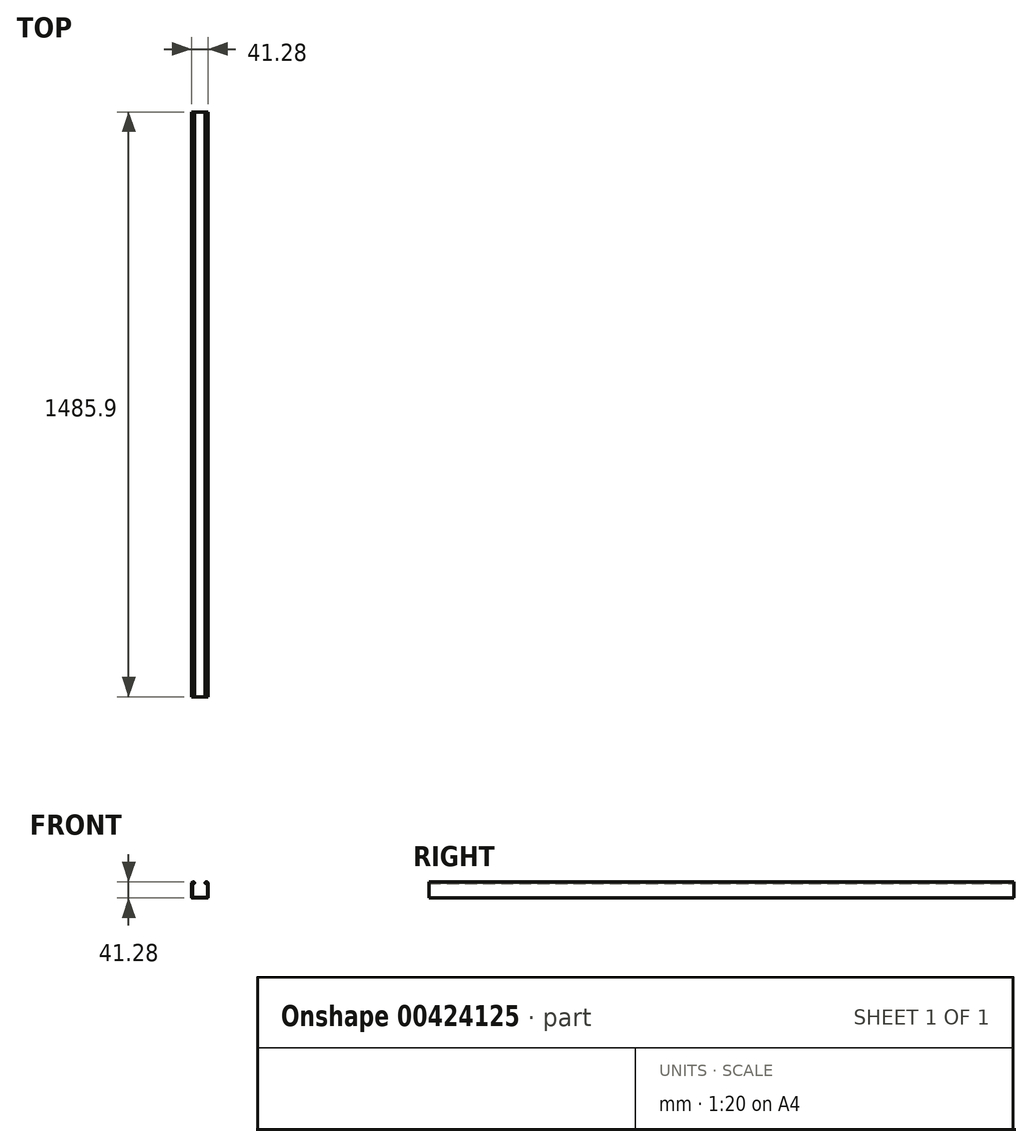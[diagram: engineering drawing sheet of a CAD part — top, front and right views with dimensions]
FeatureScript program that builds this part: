
annotation { "Feature Type Name" : "Feature", "Feature Type Description" : "" }
export const myFeature = defineFeature(function(context is Context, id is Id, definition is map)
    precondition{}
    {
        {
            var Q0;
            Q0=qCreatedBy(makeId("Front.planeOp"),FACE);
            var sketch = newSketch(context, id + "F0", { "sketchPlane" : qUnion([Q0])});
            skLineSegment(sketch, "E0.bottom", {"start": v(0, 0) * mm, "end": v(41.27, 0) * mm});
            skLineSegment(sketch, "E0.left", {"start": v(0, 0) * mm, "end": v(0, 37.31) * mm});
            skLineSegment(sketch, "E0.right", {"start": v(41.27, 0) * mm, "end": v(41.27, 37.31) * mm});
            skLineSegment(sketch, "E1.0", {"start": v(1.59, 1.59) * mm, "end": v(1.59, 37.31) * mm});
            skLineSegment(sketch, "E2.0", {"start": v(1.59, 1.59) * mm, "end": v(39.69, 1.59) * mm});
            skLineSegment(sketch, "E3.0", {"start": v(39.69, 1.59) * mm, "end": v(39.69, 37.31) * mm});
            skArc(sketch, "E4", {"start": v(7.92, 37.31) * mm, "mid": v(3.96, 41.28) * mm, "end": v(0, 37.31) * mm});
            skArc(sketch, "E5", {"start": v(6.34, 37.31) * mm, "mid": v(3.96, 39.69) * mm, "end": v(1.59, 37.31) * mm});
            skLineSegment(sketch, "E6", {"start": v(6.34, 37.31) * mm, "end": v(7.92, 37.31) * mm});
            skPoint(sketch, "E7.orphan", {"position": v(0, 41.28) * mm});
            skArc(sketch, "E8.MirrorCS", {"start": v(34.94, 37.31) * mm, "mid": v(37.31, 39.69) * mm, "end": v(39.69, 37.31) * mm});
            skArc(sketch, "E9.MirrorCS", {"start": v(33.35, 37.31) * mm, "mid": v(37.31, 41.28) * mm, "end": v(41.27, 37.31) * mm});
            skLineSegment(sketch, "E10.MirrorCS", {"start": v(34.94, 37.31) * mm, "end": v(33.35, 37.31) * mm});
            skPoint(sketch, "E11.orphan", {"position": v(20.64, 41.28) * mm});
            skPoint(sketch, "E12.orphan", {"position": v(41.27, 41.28) * mm});
            skPoint(sketch, "E13.end.orphan", {"position": v(20.64, 0) * mm});
            skSolve(sketch);
        }
        {
            var Q0;
            Q0 = qSketchRegion(id + "F0", true);
            extrude(context, id + "F1", {"entities" : qUnion([Q0]), "endBound" : BoundingType.SYMMETRIC, "depth" : 1485.9 * mm});
        }
        {
            var Q0;
            Q0=makeQuery(id+"F1.opExtrude","SWEPT_EDGE",EDGE,{"disambiguationData":[OSD([sQuery(id+"F0.wireOp",EDGE,"E1.0"),sQuery(id+"F0.wireOp",EDGE,"E2.0")])]});
            var Q1;
            Q1=makeQuery(id+"F1.opExtrude","SWEPT_EDGE",EDGE,{"disambiguationData":[OSD([sQuery(id+"F0.wireOp",EDGE,"E2.0"),sQuery(id+"F0.wireOp",EDGE,"E3.0")])]});
            var Q2;
            Q2=makeQuery(id+"F1.opExtrude","SWEPT_EDGE",EDGE,{"disambiguationData":[OSD([sQuery(id+"F0.wireOp",EDGE,"E0.bottom"),sQuery(id+"F0.wireOp",EDGE,"E0.left")])]});
            var Q3;
            Q3=makeQuery(id+"F1.opExtrude","SWEPT_EDGE",EDGE,{"disambiguationData":[OSD([sQuery(id+"F0.wireOp",EDGE,"E0.bottom"),sQuery(id+"F0.wireOp",EDGE,"E0.right")])]});
            fillet(context, id + "F2", {"entities" : qUnion([Q0, Q1, Q2, Q3]), "radius" : 1.59 * mm, "tangentPropagation" : true, "allowEdgeOverflow" : false});
        }
        {
            var Q0;
            Q0=makeQuery(id+"F1.opExtrude","SWEPT_FACE",FACE,{"disambiguationData":[OSD([sQuery(id+"F0.wireOp",EDGE,"E6")])]});
            var Q1;
            Q1=makeQuery(id+"F1.opExtrude","SWEPT_EDGE",EDGE,{"disambiguationData":[OSD([sQuery(id+"F0.wireOp",EDGE,"E5"),sQuery(id+"F0.wireOp",EDGE,"E6")])]});
            var Q2;
            Q2=makeQuery(id+"F1.opExtrude","SWEPT_EDGE",EDGE,{"disambiguationData":[OSD([sQuery(id+"F0.wireOp",EDGE,"E9.MirrorCS"),sQuery(id+"F0.wireOp",EDGE,"E10.MirrorCS")])]});
            var Q3;
            Q3=makeQuery(id+"F1.opExtrude","SWEPT_EDGE",EDGE,{"disambiguationData":[OSD([sQuery(id+"F0.wireOp",EDGE,"E8.MirrorCS"),sQuery(id+"F0.wireOp",EDGE,"E10.MirrorCS")])]});
            fillet(context, id + "F3", {"entities" : qUnion([Q0, Q1, Q2, Q3]), "radius" : 0.64 * mm, "tangentPropagation" : true, "allowEdgeOverflow" : false});
        }
    });
